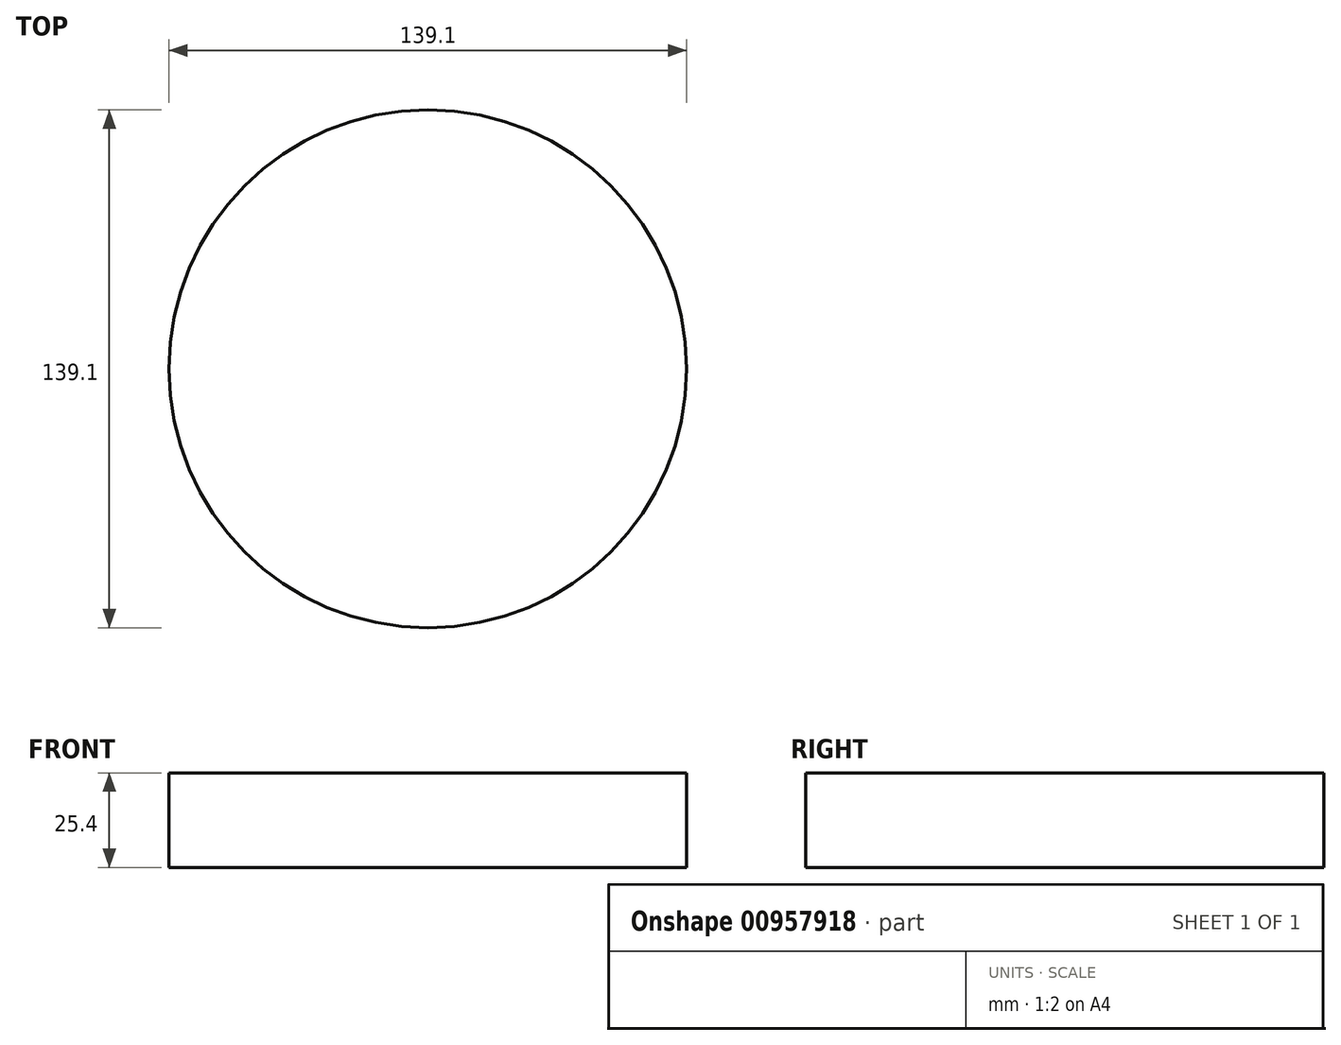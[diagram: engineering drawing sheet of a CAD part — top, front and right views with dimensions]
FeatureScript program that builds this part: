
annotation { "Feature Type Name" : "Feature", "Feature Type Description" : "" }
export const myFeature = defineFeature(function(context is Context, id is Id, definition is map)
    precondition{}
    {
        {
            var Q0;
            Q0=qCreatedBy(makeId("Top.planeOp"),FACE);
            var sketch = newSketch(context, id + "F0", { "sketchPlane" : qUnion([Q0])});
            skCircle(sketch, "E0", {"center": v(0, 0) * mm, "radius": 69.55 * mm});
            skSolve(sketch);
        }
        {
            var Q0;
            Q0=makeQuery(id+"F0.imprint","IMPRINT",FACE,{"disambiguationData":[TD([[makeQuery(id+"F0.imprint","IMPRINT",EDGE,{"derivedFrom":sQuery(id+"F0.wireOp",EDGE,"E0")}),1.0]])]});
            var Q1;
            Q1=sQuery(id+"F0.wireOp",EDGE,"E0");
            extrude(context, id + "F1", {"entities" : qUnion([Q0]), "surfaceEntities" : qUnion([Q1]), "depth" : 25.4 * mm, "offsetDistance" : 25.4 * mm});
        }
        {
            var Q0;
            Q0=sQuery(id+"F0.wireOp",EDGE,"E0");
            extrude(context, id + "F2", {"bodyType" : ToolBodyType.SURFACE, "surfaceEntities" : qUnion([Q0]), "depth" : 100 * mm, "offsetDistance" : 25.4 * mm});
        }
    });
